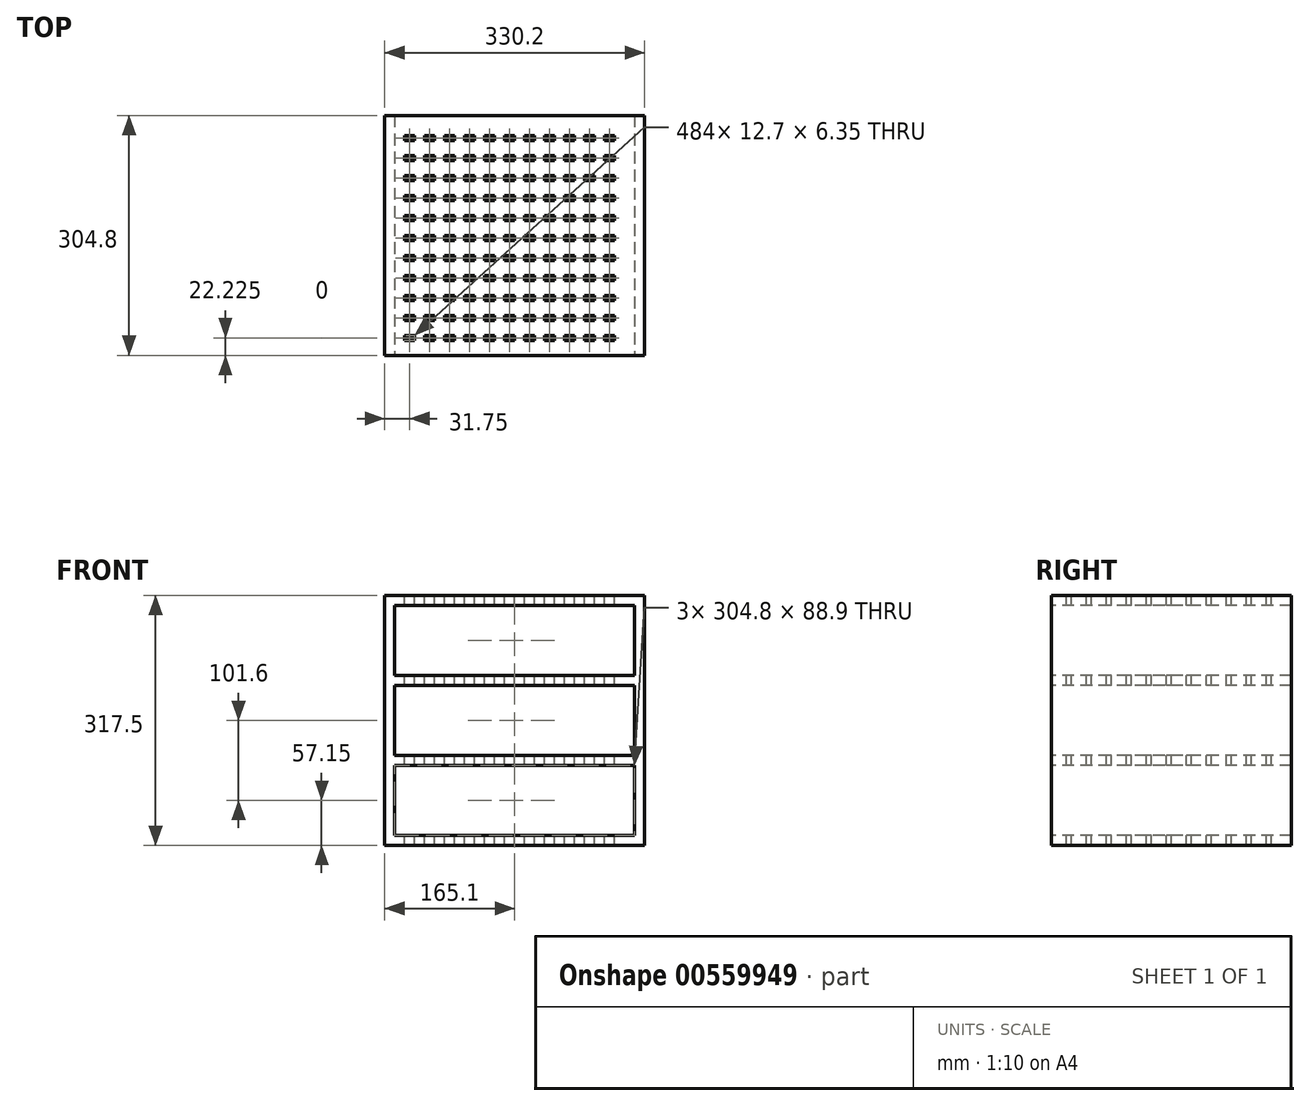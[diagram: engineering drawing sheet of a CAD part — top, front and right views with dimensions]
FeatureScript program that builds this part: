
annotation { "Feature Type Name" : "Feature", "Feature Type Description" : "" }
export const myFeature = defineFeature(function(context is Context, id is Id, definition is map)
    precondition{}
    {
        {
            var Q0;
            Q0=qCreatedBy(makeId("Front.planeOp"),FACE);
            var sketch = newSketch(context, id + "F0", { "sketchPlane" : qUnion([Q0])});
            skLineSegment(sketch, "E0.bottom", {"start": v(0, 88.9) * mm, "end": v(304.8, 88.9) * mm});
            skLineSegment(sketch, "E0.top", {"start": v(0, 0) * mm, "end": v(304.8, 0) * mm});
            skLineSegment(sketch, "E0.left", {"start": v(0, 88.9) * mm, "end": v(0, 0) * mm});
            skLineSegment(sketch, "E0.right", {"start": v(304.8, 88.9) * mm, "end": v(304.8, 0) * mm});
            skLineSegment(sketch, "E1.top", {"start": v(0, 101.6) * mm, "end": v(304.8, 101.6) * mm});
            skLineSegment(sketch, "E2.top", {"start": v(0, 190.5) * mm, "end": v(304.8, 190.5) * mm});
            skLineSegment(sketch, "E2.left", {"start": v(0, 101.6) * mm, "end": v(0, 190.5) * mm});
            skLineSegment(sketch, "E2.right", {"start": v(304.8, 101.6) * mm, "end": v(304.8, 190.5) * mm});
            skLineSegment(sketch, "E3.left", {"start": v(0, 0) * mm, "end": v(0, 88.9) * mm});
            skLineSegment(sketch, "E4.right", {"start": v(304.8, 190.5) * mm, "end": v(304.8, 101.6) * mm});
            skLineSegment(sketch, "E5.top", {"start": v(304.8, 0) * mm, "end": v(0, 0) * mm});
            skLineSegment(sketch, "E6", {"start": v(-12.7, 304.8) * mm, "end": v(-12.7, -12.7) * mm});
            skLineSegment(sketch, "E7", {"start": v(-12.7, -12.7) * mm, "end": v(317.5, -12.7) * mm});
            skLineSegment(sketch, "E8", {"start": v(317.5, -12.7) * mm, "end": v(317.5, 304.8) * mm});
            skLineSegment(sketch, "E9.bottom", {"start": v(0, 203.2) * mm, "end": v(304.8, 203.2) * mm});
            skLineSegment(sketch, "E9.top", {"start": v(0, 292.1) * mm, "end": v(304.8, 292.1) * mm});
            skLineSegment(sketch, "E9.left", {"start": v(0, 203.2) * mm, "end": v(0, 292.1) * mm});
            skLineSegment(sketch, "E9.right", {"start": v(304.8, 203.2) * mm, "end": v(304.8, 292.1) * mm});
            skLineSegment(sketch, "E10", {"start": v(-12.7, 304.8) * mm, "end": v(317.5, 304.8) * mm});
            skSolve(sketch);
        }
        {
            var Q0;
            Q0=makeQuery(id+"F0.imprint","IMPRINT",FACE,{"disambiguationData":[TD([[makeQuery(id+"F0.imprint","IMPRINT",EDGE,{"derivedFrom":sQuery(id+"F0.wireOp",EDGE,"E0.bottom")}),1.0]])]});
            extrude(context, id + "F1", {"entities" : qUnion([Q0]), "oppositeDirection" : true, "depth" : 304.8 * mm, "offsetDistance" : 25.4 * mm});
        }
        {
            var Q0;
            Q0=makeQuery(id+"F1.opExtrude","SWEPT_FACE",FACE,{"disambiguationData":[OSD([sQuery(id+"F0.wireOp",EDGE,"E10")])]});
            var sketch = newSketch(context, id + "F2", { "sketchPlane" : qUnion([Q0])});
            skLineSegment(sketch, "E11.bottom", {"start": v(12.7, 19.05) * mm, "end": v(25.4, 19.05) * mm});
            skLineSegment(sketch, "E11.top", {"start": v(12.7, 25.4) * mm, "end": v(25.4, 25.4) * mm});
            skLineSegment(sketch, "E11.left", {"start": v(12.7, 19.05) * mm, "end": v(12.7, 25.4) * mm});
            skLineSegment(sketch, "E11.right", {"start": v(25.4, 19.05) * mm, "end": v(25.4, 25.4) * mm});
            skLineSegment(sketch, "E12.0.1.0", {"start": v(12.7, 44.45) * mm, "end": v(12.7, 50.8) * mm});
            skLineSegment(sketch, "E12.0.1.1", {"start": v(12.7, 50.8) * mm, "end": v(25.4, 50.8) * mm});
            skLineSegment(sketch, "E12.0.1.2", {"start": v(25.4, 44.45) * mm, "end": v(25.4, 50.8) * mm});
            skLineSegment(sketch, "E12.0.1.3", {"start": v(12.7, 44.45) * mm, "end": v(25.4, 44.45) * mm});
            skLineSegment(sketch, "E12.0.2.0", {"start": v(12.7, 69.85) * mm, "end": v(12.7, 76.2) * mm});
            skLineSegment(sketch, "E12.0.2.1", {"start": v(12.7, 76.2) * mm, "end": v(25.4, 76.2) * mm});
            skLineSegment(sketch, "E12.0.2.2", {"start": v(25.4, 69.85) * mm, "end": v(25.4, 76.2) * mm});
            skLineSegment(sketch, "E12.0.2.3", {"start": v(12.7, 69.85) * mm, "end": v(25.4, 69.85) * mm});
            skLineSegment(sketch, "E12.0.3.0", {"start": v(12.7, 95.25) * mm, "end": v(12.7, 101.6) * mm});
            skLineSegment(sketch, "E12.0.3.1", {"start": v(12.7, 101.6) * mm, "end": v(25.4, 101.6) * mm});
            skLineSegment(sketch, "E12.0.3.2", {"start": v(25.4, 95.25) * mm, "end": v(25.4, 101.6) * mm});
            skLineSegment(sketch, "E12.0.3.3", {"start": v(12.7, 95.25) * mm, "end": v(25.4, 95.25) * mm});
            skLineSegment(sketch, "E12.0.4.0", {"start": v(12.7, 120.65) * mm, "end": v(12.7, 127) * mm});
            skLineSegment(sketch, "E12.0.4.1", {"start": v(12.7, 127) * mm, "end": v(25.4, 127) * mm});
            skLineSegment(sketch, "E12.0.4.2", {"start": v(25.4, 120.65) * mm, "end": v(25.4, 127) * mm});
            skLineSegment(sketch, "E12.0.4.3", {"start": v(12.7, 120.65) * mm, "end": v(25.4, 120.65) * mm});
            skLineSegment(sketch, "E12.0.5.0", {"start": v(12.7, 146.05) * mm, "end": v(12.7, 152.4) * mm});
            skLineSegment(sketch, "E12.0.5.1", {"start": v(12.7, 152.4) * mm, "end": v(25.4, 152.4) * mm});
            skLineSegment(sketch, "E12.0.5.2", {"start": v(25.4, 146.05) * mm, "end": v(25.4, 152.4) * mm});
            skLineSegment(sketch, "E12.0.5.3", {"start": v(12.7, 146.05) * mm, "end": v(25.4, 146.05) * mm});
            skLineSegment(sketch, "E12.0.6.0", {"start": v(12.7, 171.45) * mm, "end": v(12.7, 177.8) * mm});
            skLineSegment(sketch, "E12.0.6.1", {"start": v(12.7, 177.8) * mm, "end": v(25.4, 177.8) * mm});
            skLineSegment(sketch, "E12.0.6.2", {"start": v(25.4, 171.45) * mm, "end": v(25.4, 177.8) * mm});
            skLineSegment(sketch, "E12.0.6.3", {"start": v(12.7, 171.45) * mm, "end": v(25.4, 171.45) * mm});
            skLineSegment(sketch, "E12.0.7.0", {"start": v(12.7, 196.85) * mm, "end": v(12.7, 203.2) * mm});
            skLineSegment(sketch, "E12.0.7.1", {"start": v(12.7, 203.2) * mm, "end": v(25.4, 203.2) * mm});
            skLineSegment(sketch, "E12.0.7.2", {"start": v(25.4, 196.85) * mm, "end": v(25.4, 203.2) * mm});
            skLineSegment(sketch, "E12.0.7.3", {"start": v(12.7, 196.85) * mm, "end": v(25.4, 196.85) * mm});
            skLineSegment(sketch, "E12.0.8.0", {"start": v(12.7, 222.25) * mm, "end": v(12.7, 228.6) * mm});
            skLineSegment(sketch, "E12.0.8.1", {"start": v(12.7, 228.6) * mm, "end": v(25.4, 228.6) * mm});
            skLineSegment(sketch, "E12.0.8.2", {"start": v(25.4, 222.25) * mm, "end": v(25.4, 228.6) * mm});
            skLineSegment(sketch, "E12.0.8.3", {"start": v(12.7, 222.25) * mm, "end": v(25.4, 222.25) * mm});
            skLineSegment(sketch, "E12.0.9.0", {"start": v(12.7, 247.65) * mm, "end": v(12.7, 254) * mm});
            skLineSegment(sketch, "E12.0.9.1", {"start": v(12.7, 254) * mm, "end": v(25.4, 254) * mm});
            skLineSegment(sketch, "E12.0.9.2", {"start": v(25.4, 247.65) * mm, "end": v(25.4, 254) * mm});
            skLineSegment(sketch, "E12.0.9.3", {"start": v(12.7, 247.65) * mm, "end": v(25.4, 247.65) * mm});
            skLineSegment(sketch, "E12.0.10.0", {"start": v(12.7, 273.05) * mm, "end": v(12.7, 279.4) * mm});
            skLineSegment(sketch, "E12.0.10.1", {"start": v(12.7, 279.4) * mm, "end": v(25.4, 279.4) * mm});
            skLineSegment(sketch, "E12.0.10.2", {"start": v(25.4, 273.05) * mm, "end": v(25.4, 279.4) * mm});
            skLineSegment(sketch, "E12.0.10.3", {"start": v(12.7, 273.05) * mm, "end": v(25.4, 273.05) * mm});
            skLineSegment(sketch, "E12.1.0.0", {"start": v(38.1, 19.05) * mm, "end": v(38.1, 25.4) * mm});
            skLineSegment(sketch, "E12.1.0.1", {"start": v(38.1, 25.4) * mm, "end": v(50.8, 25.4) * mm});
            skLineSegment(sketch, "E12.1.0.2", {"start": v(50.8, 19.05) * mm, "end": v(50.8, 25.4) * mm});
            skLineSegment(sketch, "E12.1.0.3", {"start": v(38.1, 19.05) * mm, "end": v(50.8, 19.05) * mm});
            skLineSegment(sketch, "E12.1.1.0", {"start": v(38.1, 44.45) * mm, "end": v(38.1, 50.8) * mm});
            skLineSegment(sketch, "E12.1.1.1", {"start": v(38.1, 50.8) * mm, "end": v(50.8, 50.8) * mm});
            skLineSegment(sketch, "E12.1.1.2", {"start": v(50.8, 44.45) * mm, "end": v(50.8, 50.8) * mm});
            skLineSegment(sketch, "E12.1.1.3", {"start": v(38.1, 44.45) * mm, "end": v(50.8, 44.45) * mm});
            skLineSegment(sketch, "E12.1.2.0", {"start": v(38.1, 69.85) * mm, "end": v(38.1, 76.2) * mm});
            skLineSegment(sketch, "E12.1.2.1", {"start": v(38.1, 76.2) * mm, "end": v(50.8, 76.2) * mm});
            skLineSegment(sketch, "E12.1.2.2", {"start": v(50.8, 69.85) * mm, "end": v(50.8, 76.2) * mm});
            skLineSegment(sketch, "E12.1.2.3", {"start": v(38.1, 69.85) * mm, "end": v(50.8, 69.85) * mm});
            skLineSegment(sketch, "E12.1.3.0", {"start": v(38.1, 95.25) * mm, "end": v(38.1, 101.6) * mm});
            skLineSegment(sketch, "E12.1.3.1", {"start": v(38.1, 101.6) * mm, "end": v(50.8, 101.6) * mm});
            skLineSegment(sketch, "E12.1.3.2", {"start": v(50.8, 95.25) * mm, "end": v(50.8, 101.6) * mm});
            skLineSegment(sketch, "E12.1.3.3", {"start": v(38.1, 95.25) * mm, "end": v(50.8, 95.25) * mm});
            skLineSegment(sketch, "E12.1.4.0", {"start": v(38.1, 120.65) * mm, "end": v(38.1, 127) * mm});
            skLineSegment(sketch, "E12.1.4.1", {"start": v(38.1, 127) * mm, "end": v(50.8, 127) * mm});
            skLineSegment(sketch, "E12.1.4.2", {"start": v(50.8, 120.65) * mm, "end": v(50.8, 127) * mm});
            skLineSegment(sketch, "E12.1.4.3", {"start": v(38.1, 120.65) * mm, "end": v(50.8, 120.65) * mm});
            skLineSegment(sketch, "E12.1.5.0", {"start": v(38.1, 146.05) * mm, "end": v(38.1, 152.4) * mm});
            skLineSegment(sketch, "E12.1.5.1", {"start": v(38.1, 152.4) * mm, "end": v(50.8, 152.4) * mm});
            skLineSegment(sketch, "E12.1.5.2", {"start": v(50.8, 146.05) * mm, "end": v(50.8, 152.4) * mm});
            skLineSegment(sketch, "E12.1.5.3", {"start": v(38.1, 146.05) * mm, "end": v(50.8, 146.05) * mm});
            skLineSegment(sketch, "E12.1.6.0", {"start": v(38.1, 171.45) * mm, "end": v(38.1, 177.8) * mm});
            skLineSegment(sketch, "E12.1.6.1", {"start": v(38.1, 177.8) * mm, "end": v(50.8, 177.8) * mm});
            skLineSegment(sketch, "E12.1.6.2", {"start": v(50.8, 171.45) * mm, "end": v(50.8, 177.8) * mm});
            skLineSegment(sketch, "E12.1.6.3", {"start": v(38.1, 171.45) * mm, "end": v(50.8, 171.45) * mm});
            skLineSegment(sketch, "E12.1.7.0", {"start": v(38.1, 196.85) * mm, "end": v(38.1, 203.2) * mm});
            skLineSegment(sketch, "E12.1.7.1", {"start": v(38.1, 203.2) * mm, "end": v(50.8, 203.2) * mm});
            skLineSegment(sketch, "E12.1.7.2", {"start": v(50.8, 196.85) * mm, "end": v(50.8, 203.2) * mm});
            skLineSegment(sketch, "E12.1.7.3", {"start": v(38.1, 196.85) * mm, "end": v(50.8, 196.85) * mm});
            skLineSegment(sketch, "E12.1.8.0", {"start": v(38.1, 222.25) * mm, "end": v(38.1, 228.6) * mm});
            skLineSegment(sketch, "E12.1.8.1", {"start": v(38.1, 228.6) * mm, "end": v(50.8, 228.6) * mm});
            skLineSegment(sketch, "E12.1.8.2", {"start": v(50.8, 222.25) * mm, "end": v(50.8, 228.6) * mm});
            skLineSegment(sketch, "E12.1.8.3", {"start": v(38.1, 222.25) * mm, "end": v(50.8, 222.25) * mm});
            skLineSegment(sketch, "E12.1.9.0", {"start": v(38.1, 247.65) * mm, "end": v(38.1, 254) * mm});
            skLineSegment(sketch, "E12.1.9.1", {"start": v(38.1, 254) * mm, "end": v(50.8, 254) * mm});
            skLineSegment(sketch, "E12.1.9.2", {"start": v(50.8, 247.65) * mm, "end": v(50.8, 254) * mm});
            skLineSegment(sketch, "E12.1.9.3", {"start": v(38.1, 247.65) * mm, "end": v(50.8, 247.65) * mm});
            skLineSegment(sketch, "E12.1.10.0", {"start": v(38.1, 273.05) * mm, "end": v(38.1, 279.4) * mm});
            skLineSegment(sketch, "E12.1.10.1", {"start": v(38.1, 279.4) * mm, "end": v(50.8, 279.4) * mm});
            skLineSegment(sketch, "E12.1.10.2", {"start": v(50.8, 273.05) * mm, "end": v(50.8, 279.4) * mm});
            skLineSegment(sketch, "E12.1.10.3", {"start": v(38.1, 273.05) * mm, "end": v(50.8, 273.05) * mm});
            skLineSegment(sketch, "E12.2.0.0", {"start": v(63.5, 19.05) * mm, "end": v(63.5, 25.4) * mm});
            skLineSegment(sketch, "E12.2.0.1", {"start": v(63.5, 25.4) * mm, "end": v(76.2, 25.4) * mm});
            skLineSegment(sketch, "E12.2.0.2", {"start": v(76.2, 19.05) * mm, "end": v(76.2, 25.4) * mm});
            skLineSegment(sketch, "E12.2.0.3", {"start": v(63.5, 19.05) * mm, "end": v(76.2, 19.05) * mm});
            skLineSegment(sketch, "E12.2.1.0", {"start": v(63.5, 44.45) * mm, "end": v(63.5, 50.8) * mm});
            skLineSegment(sketch, "E12.2.1.1", {"start": v(63.5, 50.8) * mm, "end": v(76.2, 50.8) * mm});
            skLineSegment(sketch, "E12.2.1.2", {"start": v(76.2, 44.45) * mm, "end": v(76.2, 50.8) * mm});
            skLineSegment(sketch, "E12.2.1.3", {"start": v(63.5, 44.45) * mm, "end": v(76.2, 44.45) * mm});
            skLineSegment(sketch, "E12.2.2.0", {"start": v(63.5, 69.85) * mm, "end": v(63.5, 76.2) * mm});
            skLineSegment(sketch, "E12.2.2.1", {"start": v(63.5, 76.2) * mm, "end": v(76.2, 76.2) * mm});
            skLineSegment(sketch, "E12.2.2.2", {"start": v(76.2, 69.85) * mm, "end": v(76.2, 76.2) * mm});
            skLineSegment(sketch, "E12.2.2.3", {"start": v(63.5, 69.85) * mm, "end": v(76.2, 69.85) * mm});
            skLineSegment(sketch, "E12.2.3.0", {"start": v(63.5, 95.25) * mm, "end": v(63.5, 101.6) * mm});
            skLineSegment(sketch, "E12.2.3.1", {"start": v(63.5, 101.6) * mm, "end": v(76.2, 101.6) * mm});
            skLineSegment(sketch, "E12.2.3.2", {"start": v(76.2, 95.25) * mm, "end": v(76.2, 101.6) * mm});
            skLineSegment(sketch, "E12.2.3.3", {"start": v(63.5, 95.25) * mm, "end": v(76.2, 95.25) * mm});
            skLineSegment(sketch, "E12.2.4.0", {"start": v(63.5, 120.65) * mm, "end": v(63.5, 127) * mm});
            skLineSegment(sketch, "E12.2.4.1", {"start": v(63.5, 127) * mm, "end": v(76.2, 127) * mm});
            skLineSegment(sketch, "E12.2.4.2", {"start": v(76.2, 120.65) * mm, "end": v(76.2, 127) * mm});
            skLineSegment(sketch, "E12.2.4.3", {"start": v(63.5, 120.65) * mm, "end": v(76.2, 120.65) * mm});
            skLineSegment(sketch, "E12.2.5.0", {"start": v(63.5, 146.05) * mm, "end": v(63.5, 152.4) * mm});
            skLineSegment(sketch, "E12.2.5.1", {"start": v(63.5, 152.4) * mm, "end": v(76.2, 152.4) * mm});
            skLineSegment(sketch, "E12.2.5.2", {"start": v(76.2, 146.05) * mm, "end": v(76.2, 152.4) * mm});
            skLineSegment(sketch, "E12.2.5.3", {"start": v(63.5, 146.05) * mm, "end": v(76.2, 146.05) * mm});
            skLineSegment(sketch, "E12.2.6.0", {"start": v(63.5, 171.45) * mm, "end": v(63.5, 177.8) * mm});
            skLineSegment(sketch, "E12.2.6.1", {"start": v(63.5, 177.8) * mm, "end": v(76.2, 177.8) * mm});
            skLineSegment(sketch, "E12.2.6.2", {"start": v(76.2, 171.45) * mm, "end": v(76.2, 177.8) * mm});
            skLineSegment(sketch, "E12.2.6.3", {"start": v(63.5, 171.45) * mm, "end": v(76.2, 171.45) * mm});
            skLineSegment(sketch, "E12.2.7.0", {"start": v(63.5, 196.85) * mm, "end": v(63.5, 203.2) * mm});
            skLineSegment(sketch, "E12.2.7.1", {"start": v(63.5, 203.2) * mm, "end": v(76.2, 203.2) * mm});
            skLineSegment(sketch, "E12.2.7.2", {"start": v(76.2, 196.85) * mm, "end": v(76.2, 203.2) * mm});
            skLineSegment(sketch, "E12.2.7.3", {"start": v(63.5, 196.85) * mm, "end": v(76.2, 196.85) * mm});
            skLineSegment(sketch, "E12.2.8.0", {"start": v(63.5, 222.25) * mm, "end": v(63.5, 228.6) * mm});
            skLineSegment(sketch, "E12.2.8.1", {"start": v(63.5, 228.6) * mm, "end": v(76.2, 228.6) * mm});
            skLineSegment(sketch, "E12.2.8.2", {"start": v(76.2, 222.25) * mm, "end": v(76.2, 228.6) * mm});
            skLineSegment(sketch, "E12.2.8.3", {"start": v(63.5, 222.25) * mm, "end": v(76.2, 222.25) * mm});
            skLineSegment(sketch, "E12.2.9.0", {"start": v(63.5, 247.65) * mm, "end": v(63.5, 254) * mm});
            skLineSegment(sketch, "E12.2.9.1", {"start": v(63.5, 254) * mm, "end": v(76.2, 254) * mm});
            skLineSegment(sketch, "E12.2.9.2", {"start": v(76.2, 247.65) * mm, "end": v(76.2, 254) * mm});
            skLineSegment(sketch, "E12.2.9.3", {"start": v(63.5, 247.65) * mm, "end": v(76.2, 247.65) * mm});
            skLineSegment(sketch, "E12.2.10.0", {"start": v(63.5, 273.05) * mm, "end": v(63.5, 279.4) * mm});
            skLineSegment(sketch, "E12.2.10.1", {"start": v(63.5, 279.4) * mm, "end": v(76.2, 279.4) * mm});
            skLineSegment(sketch, "E12.2.10.2", {"start": v(76.2, 273.05) * mm, "end": v(76.2, 279.4) * mm});
            skLineSegment(sketch, "E12.2.10.3", {"start": v(63.5, 273.05) * mm, "end": v(76.2, 273.05) * mm});
            skLineSegment(sketch, "E12.3.0.0", {"start": v(88.9, 19.05) * mm, "end": v(88.9, 25.4) * mm});
            skLineSegment(sketch, "E12.3.0.1", {"start": v(88.9, 25.4) * mm, "end": v(101.6, 25.4) * mm});
            skLineSegment(sketch, "E12.3.0.2", {"start": v(101.6, 19.05) * mm, "end": v(101.6, 25.4) * mm});
            skLineSegment(sketch, "E12.3.0.3", {"start": v(88.9, 19.05) * mm, "end": v(101.6, 19.05) * mm});
            skLineSegment(sketch, "E12.3.1.0", {"start": v(88.9, 44.45) * mm, "end": v(88.9, 50.8) * mm});
            skLineSegment(sketch, "E12.3.1.1", {"start": v(88.9, 50.8) * mm, "end": v(101.6, 50.8) * mm});
            skLineSegment(sketch, "E12.3.1.2", {"start": v(101.6, 44.45) * mm, "end": v(101.6, 50.8) * mm});
            skLineSegment(sketch, "E12.3.1.3", {"start": v(88.9, 44.45) * mm, "end": v(101.6, 44.45) * mm});
            skLineSegment(sketch, "E12.3.2.0", {"start": v(88.9, 69.85) * mm, "end": v(88.9, 76.2) * mm});
            skLineSegment(sketch, "E12.3.2.1", {"start": v(88.9, 76.2) * mm, "end": v(101.6, 76.2) * mm});
            skLineSegment(sketch, "E12.3.2.2", {"start": v(101.6, 69.85) * mm, "end": v(101.6, 76.2) * mm});
            skLineSegment(sketch, "E12.3.2.3", {"start": v(88.9, 69.85) * mm, "end": v(101.6, 69.85) * mm});
            skLineSegment(sketch, "E12.3.3.0", {"start": v(88.9, 95.25) * mm, "end": v(88.9, 101.6) * mm});
            skLineSegment(sketch, "E12.3.3.1", {"start": v(88.9, 101.6) * mm, "end": v(101.6, 101.6) * mm});
            skLineSegment(sketch, "E12.3.3.2", {"start": v(101.6, 95.25) * mm, "end": v(101.6, 101.6) * mm});
            skLineSegment(sketch, "E12.3.3.3", {"start": v(88.9, 95.25) * mm, "end": v(101.6, 95.25) * mm});
            skLineSegment(sketch, "E12.3.4.0", {"start": v(88.9, 120.65) * mm, "end": v(88.9, 127) * mm});
            skLineSegment(sketch, "E12.3.4.1", {"start": v(88.9, 127) * mm, "end": v(101.6, 127) * mm});
            skLineSegment(sketch, "E12.3.4.2", {"start": v(101.6, 120.65) * mm, "end": v(101.6, 127) * mm});
            skLineSegment(sketch, "E12.3.4.3", {"start": v(88.9, 120.65) * mm, "end": v(101.6, 120.65) * mm});
            skLineSegment(sketch, "E12.3.5.0", {"start": v(88.9, 146.05) * mm, "end": v(88.9, 152.4) * mm});
            skLineSegment(sketch, "E12.3.5.1", {"start": v(88.9, 152.4) * mm, "end": v(101.6, 152.4) * mm});
            skLineSegment(sketch, "E12.3.5.2", {"start": v(101.6, 146.05) * mm, "end": v(101.6, 152.4) * mm});
            skLineSegment(sketch, "E12.3.5.3", {"start": v(88.9, 146.05) * mm, "end": v(101.6, 146.05) * mm});
            skLineSegment(sketch, "E12.3.6.0", {"start": v(88.9, 171.45) * mm, "end": v(88.9, 177.8) * mm});
            skLineSegment(sketch, "E12.3.6.1", {"start": v(88.9, 177.8) * mm, "end": v(101.6, 177.8) * mm});
            skLineSegment(sketch, "E12.3.6.2", {"start": v(101.6, 171.45) * mm, "end": v(101.6, 177.8) * mm});
            skLineSegment(sketch, "E12.3.6.3", {"start": v(88.9, 171.45) * mm, "end": v(101.6, 171.45) * mm});
            skLineSegment(sketch, "E12.3.7.0", {"start": v(88.9, 196.85) * mm, "end": v(88.9, 203.2) * mm});
            skLineSegment(sketch, "E12.3.7.1", {"start": v(88.9, 203.2) * mm, "end": v(101.6, 203.2) * mm});
            skLineSegment(sketch, "E12.3.7.2", {"start": v(101.6, 196.85) * mm, "end": v(101.6, 203.2) * mm});
            skLineSegment(sketch, "E12.3.7.3", {"start": v(88.9, 196.85) * mm, "end": v(101.6, 196.85) * mm});
            skLineSegment(sketch, "E12.3.8.0", {"start": v(88.9, 222.25) * mm, "end": v(88.9, 228.6) * mm});
            skLineSegment(sketch, "E12.3.8.1", {"start": v(88.9, 228.6) * mm, "end": v(101.6, 228.6) * mm});
            skLineSegment(sketch, "E12.3.8.2", {"start": v(101.6, 222.25) * mm, "end": v(101.6, 228.6) * mm});
            skLineSegment(sketch, "E12.3.8.3", {"start": v(88.9, 222.25) * mm, "end": v(101.6, 222.25) * mm});
            skLineSegment(sketch, "E12.3.9.0", {"start": v(88.9, 247.65) * mm, "end": v(88.9, 254) * mm});
            skLineSegment(sketch, "E12.3.9.1", {"start": v(88.9, 254) * mm, "end": v(101.6, 254) * mm});
            skLineSegment(sketch, "E12.3.9.2", {"start": v(101.6, 247.65) * mm, "end": v(101.6, 254) * mm});
            skLineSegment(sketch, "E12.3.9.3", {"start": v(88.9, 247.65) * mm, "end": v(101.6, 247.65) * mm});
            skLineSegment(sketch, "E12.3.10.0", {"start": v(88.9, 273.05) * mm, "end": v(88.9, 279.4) * mm});
            skLineSegment(sketch, "E12.3.10.1", {"start": v(88.9, 279.4) * mm, "end": v(101.6, 279.4) * mm});
            skLineSegment(sketch, "E12.3.10.2", {"start": v(101.6, 273.05) * mm, "end": v(101.6, 279.4) * mm});
            skLineSegment(sketch, "E12.3.10.3", {"start": v(88.9, 273.05) * mm, "end": v(101.6, 273.05) * mm});
            skLineSegment(sketch, "E12.4.0.0", {"start": v(114.3, 19.05) * mm, "end": v(114.3, 25.4) * mm});
            skLineSegment(sketch, "E12.4.0.1", {"start": v(114.3, 25.4) * mm, "end": v(127, 25.4) * mm});
            skLineSegment(sketch, "E12.4.0.2", {"start": v(127, 19.05) * mm, "end": v(127, 25.4) * mm});
            skLineSegment(sketch, "E12.4.0.3", {"start": v(114.3, 19.05) * mm, "end": v(127, 19.05) * mm});
            skLineSegment(sketch, "E12.4.1.0", {"start": v(114.3, 44.45) * mm, "end": v(114.3, 50.8) * mm});
            skLineSegment(sketch, "E12.4.1.1", {"start": v(114.3, 50.8) * mm, "end": v(127, 50.8) * mm});
            skLineSegment(sketch, "E12.4.1.2", {"start": v(127, 44.45) * mm, "end": v(127, 50.8) * mm});
            skLineSegment(sketch, "E12.4.1.3", {"start": v(114.3, 44.45) * mm, "end": v(127, 44.45) * mm});
            skLineSegment(sketch, "E12.4.2.0", {"start": v(114.3, 69.85) * mm, "end": v(114.3, 76.2) * mm});
            skLineSegment(sketch, "E12.4.2.1", {"start": v(114.3, 76.2) * mm, "end": v(127, 76.2) * mm});
            skLineSegment(sketch, "E12.4.2.2", {"start": v(127, 69.85) * mm, "end": v(127, 76.2) * mm});
            skLineSegment(sketch, "E12.4.2.3", {"start": v(114.3, 69.85) * mm, "end": v(127, 69.85) * mm});
            skLineSegment(sketch, "E12.4.3.0", {"start": v(114.3, 95.25) * mm, "end": v(114.3, 101.6) * mm});
            skLineSegment(sketch, "E12.4.3.1", {"start": v(114.3, 101.6) * mm, "end": v(127, 101.6) * mm});
            skLineSegment(sketch, "E12.4.3.2", {"start": v(127, 95.25) * mm, "end": v(127, 101.6) * mm});
            skLineSegment(sketch, "E12.4.3.3", {"start": v(114.3, 95.25) * mm, "end": v(127, 95.25) * mm});
            skLineSegment(sketch, "E12.4.4.0", {"start": v(114.3, 120.65) * mm, "end": v(114.3, 127) * mm});
            skLineSegment(sketch, "E12.4.4.1", {"start": v(114.3, 127) * mm, "end": v(127, 127) * mm});
            skLineSegment(sketch, "E12.4.4.2", {"start": v(127, 120.65) * mm, "end": v(127, 127) * mm});
            skLineSegment(sketch, "E12.4.4.3", {"start": v(114.3, 120.65) * mm, "end": v(127, 120.65) * mm});
            skLineSegment(sketch, "E12.4.5.0", {"start": v(114.3, 146.05) * mm, "end": v(114.3, 152.4) * mm});
            skLineSegment(sketch, "E12.4.5.1", {"start": v(114.3, 152.4) * mm, "end": v(127, 152.4) * mm});
            skLineSegment(sketch, "E12.4.5.2", {"start": v(127, 146.05) * mm, "end": v(127, 152.4) * mm});
            skLineSegment(sketch, "E12.4.5.3", {"start": v(114.3, 146.05) * mm, "end": v(127, 146.05) * mm});
            skLineSegment(sketch, "E12.4.6.0", {"start": v(114.3, 171.45) * mm, "end": v(114.3, 177.8) * mm});
            skLineSegment(sketch, "E12.4.6.1", {"start": v(114.3, 177.8) * mm, "end": v(127, 177.8) * mm});
            skLineSegment(sketch, "E12.4.6.2", {"start": v(127, 171.45) * mm, "end": v(127, 177.8) * mm});
            skLineSegment(sketch, "E12.4.6.3", {"start": v(114.3, 171.45) * mm, "end": v(127, 171.45) * mm});
            skLineSegment(sketch, "E12.4.7.0", {"start": v(114.3, 196.85) * mm, "end": v(114.3, 203.2) * mm});
            skLineSegment(sketch, "E12.4.7.1", {"start": v(114.3, 203.2) * mm, "end": v(127, 203.2) * mm});
            skLineSegment(sketch, "E12.4.7.2", {"start": v(127, 196.85) * mm, "end": v(127, 203.2) * mm});
            skLineSegment(sketch, "E12.4.7.3", {"start": v(114.3, 196.85) * mm, "end": v(127, 196.85) * mm});
            skLineSegment(sketch, "E12.4.8.0", {"start": v(114.3, 222.25) * mm, "end": v(114.3, 228.6) * mm});
            skLineSegment(sketch, "E12.4.8.1", {"start": v(114.3, 228.6) * mm, "end": v(127, 228.6) * mm});
            skLineSegment(sketch, "E12.4.8.2", {"start": v(127, 222.25) * mm, "end": v(127, 228.6) * mm});
            skLineSegment(sketch, "E12.4.8.3", {"start": v(114.3, 222.25) * mm, "end": v(127, 222.25) * mm});
            skLineSegment(sketch, "E12.4.9.0", {"start": v(114.3, 247.65) * mm, "end": v(114.3, 254) * mm});
            skLineSegment(sketch, "E12.4.9.1", {"start": v(114.3, 254) * mm, "end": v(127, 254) * mm});
            skLineSegment(sketch, "E12.4.9.2", {"start": v(127, 247.65) * mm, "end": v(127, 254) * mm});
            skLineSegment(sketch, "E12.4.9.3", {"start": v(114.3, 247.65) * mm, "end": v(127, 247.65) * mm});
            skLineSegment(sketch, "E12.4.10.0", {"start": v(114.3, 273.05) * mm, "end": v(114.3, 279.4) * mm});
            skLineSegment(sketch, "E12.4.10.1", {"start": v(114.3, 279.4) * mm, "end": v(127, 279.4) * mm});
            skLineSegment(sketch, "E12.4.10.2", {"start": v(127, 273.05) * mm, "end": v(127, 279.4) * mm});
            skLineSegment(sketch, "E12.4.10.3", {"start": v(114.3, 273.05) * mm, "end": v(127, 273.05) * mm});
            skLineSegment(sketch, "E12.5.0.0", {"start": v(139.7, 19.05) * mm, "end": v(139.7, 25.4) * mm});
            skLineSegment(sketch, "E12.5.0.1", {"start": v(139.7, 25.4) * mm, "end": v(152.4, 25.4) * mm});
            skLineSegment(sketch, "E12.5.0.2", {"start": v(152.4, 19.05) * mm, "end": v(152.4, 25.4) * mm});
            skLineSegment(sketch, "E12.5.0.3", {"start": v(139.7, 19.05) * mm, "end": v(152.4, 19.05) * mm});
            skLineSegment(sketch, "E12.5.1.0", {"start": v(139.7, 44.45) * mm, "end": v(139.7, 50.8) * mm});
            skLineSegment(sketch, "E12.5.1.1", {"start": v(139.7, 50.8) * mm, "end": v(152.4, 50.8) * mm});
            skLineSegment(sketch, "E12.5.1.2", {"start": v(152.4, 44.45) * mm, "end": v(152.4, 50.8) * mm});
            skLineSegment(sketch, "E12.5.1.3", {"start": v(139.7, 44.45) * mm, "end": v(152.4, 44.45) * mm});
            skLineSegment(sketch, "E12.5.2.0", {"start": v(139.7, 69.85) * mm, "end": v(139.7, 76.2) * mm});
            skLineSegment(sketch, "E12.5.2.1", {"start": v(139.7, 76.2) * mm, "end": v(152.4, 76.2) * mm});
            skLineSegment(sketch, "E12.5.2.2", {"start": v(152.4, 69.85) * mm, "end": v(152.4, 76.2) * mm});
            skLineSegment(sketch, "E12.5.2.3", {"start": v(139.7, 69.85) * mm, "end": v(152.4, 69.85) * mm});
            skLineSegment(sketch, "E12.5.3.0", {"start": v(139.7, 95.25) * mm, "end": v(139.7, 101.6) * mm});
            skLineSegment(sketch, "E12.5.3.1", {"start": v(139.7, 101.6) * mm, "end": v(152.4, 101.6) * mm});
            skLineSegment(sketch, "E12.5.3.2", {"start": v(152.4, 95.25) * mm, "end": v(152.4, 101.6) * mm});
            skLineSegment(sketch, "E12.5.3.3", {"start": v(139.7, 95.25) * mm, "end": v(152.4, 95.25) * mm});
            skLineSegment(sketch, "E12.5.4.0", {"start": v(139.7, 120.65) * mm, "end": v(139.7, 127) * mm});
            skLineSegment(sketch, "E12.5.4.1", {"start": v(139.7, 127) * mm, "end": v(152.4, 127) * mm});
            skLineSegment(sketch, "E12.5.4.2", {"start": v(152.4, 120.65) * mm, "end": v(152.4, 127) * mm});
            skLineSegment(sketch, "E12.5.4.3", {"start": v(139.7, 120.65) * mm, "end": v(152.4, 120.65) * mm});
            skLineSegment(sketch, "E12.5.5.0", {"start": v(139.7, 146.05) * mm, "end": v(139.7, 152.4) * mm});
            skLineSegment(sketch, "E12.5.5.1", {"start": v(139.7, 152.4) * mm, "end": v(152.4, 152.4) * mm});
            skLineSegment(sketch, "E12.5.5.2", {"start": v(152.4, 146.05) * mm, "end": v(152.4, 152.4) * mm});
            skLineSegment(sketch, "E12.5.5.3", {"start": v(139.7, 146.05) * mm, "end": v(152.4, 146.05) * mm});
            skLineSegment(sketch, "E12.5.6.0", {"start": v(139.7, 171.45) * mm, "end": v(139.7, 177.8) * mm});
            skLineSegment(sketch, "E12.5.6.1", {"start": v(139.7, 177.8) * mm, "end": v(152.4, 177.8) * mm});
            skLineSegment(sketch, "E12.5.6.2", {"start": v(152.4, 171.45) * mm, "end": v(152.4, 177.8) * mm});
            skLineSegment(sketch, "E12.5.6.3", {"start": v(139.7, 171.45) * mm, "end": v(152.4, 171.45) * mm});
            skLineSegment(sketch, "E12.5.7.0", {"start": v(139.7, 196.85) * mm, "end": v(139.7, 203.2) * mm});
            skLineSegment(sketch, "E12.5.7.1", {"start": v(139.7, 203.2) * mm, "end": v(152.4, 203.2) * mm});
            skLineSegment(sketch, "E12.5.7.2", {"start": v(152.4, 196.85) * mm, "end": v(152.4, 203.2) * mm});
            skLineSegment(sketch, "E12.5.7.3", {"start": v(139.7, 196.85) * mm, "end": v(152.4, 196.85) * mm});
            skLineSegment(sketch, "E12.5.8.0", {"start": v(139.7, 222.25) * mm, "end": v(139.7, 228.6) * mm});
            skLineSegment(sketch, "E12.5.8.1", {"start": v(139.7, 228.6) * mm, "end": v(152.4, 228.6) * mm});
            skLineSegment(sketch, "E12.5.8.2", {"start": v(152.4, 222.25) * mm, "end": v(152.4, 228.6) * mm});
            skLineSegment(sketch, "E12.5.8.3", {"start": v(139.7, 222.25) * mm, "end": v(152.4, 222.25) * mm});
            skLineSegment(sketch, "E12.5.9.0", {"start": v(139.7, 247.65) * mm, "end": v(139.7, 254) * mm});
            skLineSegment(sketch, "E12.5.9.1", {"start": v(139.7, 254) * mm, "end": v(152.4, 254) * mm});
            skLineSegment(sketch, "E12.5.9.2", {"start": v(152.4, 247.65) * mm, "end": v(152.4, 254) * mm});
            skLineSegment(sketch, "E12.5.9.3", {"start": v(139.7, 247.65) * mm, "end": v(152.4, 247.65) * mm});
            skLineSegment(sketch, "E12.5.10.0", {"start": v(139.7, 273.05) * mm, "end": v(139.7, 279.4) * mm});
            skLineSegment(sketch, "E12.5.10.1", {"start": v(139.7, 279.4) * mm, "end": v(152.4, 279.4) * mm});
            skLineSegment(sketch, "E12.5.10.2", {"start": v(152.4, 273.05) * mm, "end": v(152.4, 279.4) * mm});
            skLineSegment(sketch, "E12.5.10.3", {"start": v(139.7, 273.05) * mm, "end": v(152.4, 273.05) * mm});
            skLineSegment(sketch, "E12.6.0.0", {"start": v(165.1, 19.05) * mm, "end": v(165.1, 25.4) * mm});
            skLineSegment(sketch, "E12.6.0.1", {"start": v(165.1, 25.4) * mm, "end": v(177.8, 25.4) * mm});
            skLineSegment(sketch, "E12.6.0.2", {"start": v(177.8, 19.05) * mm, "end": v(177.8, 25.4) * mm});
            skLineSegment(sketch, "E12.6.0.3", {"start": v(165.1, 19.05) * mm, "end": v(177.8, 19.05) * mm});
            skLineSegment(sketch, "E12.6.1.0", {"start": v(165.1, 44.45) * mm, "end": v(165.1, 50.8) * mm});
            skLineSegment(sketch, "E12.6.1.1", {"start": v(165.1, 50.8) * mm, "end": v(177.8, 50.8) * mm});
            skLineSegment(sketch, "E12.6.1.2", {"start": v(177.8, 44.45) * mm, "end": v(177.8, 50.8) * mm});
            skLineSegment(sketch, "E12.6.1.3", {"start": v(165.1, 44.45) * mm, "end": v(177.8, 44.45) * mm});
            skLineSegment(sketch, "E12.6.2.0", {"start": v(165.1, 69.85) * mm, "end": v(165.1, 76.2) * mm});
            skLineSegment(sketch, "E12.6.2.1", {"start": v(165.1, 76.2) * mm, "end": v(177.8, 76.2) * mm});
            skLineSegment(sketch, "E12.6.2.2", {"start": v(177.8, 69.85) * mm, "end": v(177.8, 76.2) * mm});
            skLineSegment(sketch, "E12.6.2.3", {"start": v(165.1, 69.85) * mm, "end": v(177.8, 69.85) * mm});
            skLineSegment(sketch, "E12.6.3.0", {"start": v(165.1, 95.25) * mm, "end": v(165.1, 101.6) * mm});
            skLineSegment(sketch, "E12.6.3.1", {"start": v(165.1, 101.6) * mm, "end": v(177.8, 101.6) * mm});
            skLineSegment(sketch, "E12.6.3.2", {"start": v(177.8, 95.25) * mm, "end": v(177.8, 101.6) * mm});
            skLineSegment(sketch, "E12.6.3.3", {"start": v(165.1, 95.25) * mm, "end": v(177.8, 95.25) * mm});
            skLineSegment(sketch, "E12.6.4.0", {"start": v(165.1, 120.65) * mm, "end": v(165.1, 127) * mm});
            skLineSegment(sketch, "E12.6.4.1", {"start": v(165.1, 127) * mm, "end": v(177.8, 127) * mm});
            skLineSegment(sketch, "E12.6.4.2", {"start": v(177.8, 120.65) * mm, "end": v(177.8, 127) * mm});
            skLineSegment(sketch, "E12.6.4.3", {"start": v(165.1, 120.65) * mm, "end": v(177.8, 120.65) * mm});
            skLineSegment(sketch, "E12.6.5.0", {"start": v(165.1, 146.05) * mm, "end": v(165.1, 152.4) * mm});
            skLineSegment(sketch, "E12.6.5.1", {"start": v(165.1, 152.4) * mm, "end": v(177.8, 152.4) * mm});
            skLineSegment(sketch, "E12.6.5.2", {"start": v(177.8, 146.05) * mm, "end": v(177.8, 152.4) * mm});
            skLineSegment(sketch, "E12.6.5.3", {"start": v(165.1, 146.05) * mm, "end": v(177.8, 146.05) * mm});
            skLineSegment(sketch, "E12.6.6.0", {"start": v(165.1, 171.45) * mm, "end": v(165.1, 177.8) * mm});
            skLineSegment(sketch, "E12.6.6.1", {"start": v(165.1, 177.8) * mm, "end": v(177.8, 177.8) * mm});
            skLineSegment(sketch, "E12.6.6.2", {"start": v(177.8, 171.45) * mm, "end": v(177.8, 177.8) * mm});
            skLineSegment(sketch, "E12.6.6.3", {"start": v(165.1, 171.45) * mm, "end": v(177.8, 171.45) * mm});
            skLineSegment(sketch, "E12.6.7.0", {"start": v(165.1, 196.85) * mm, "end": v(165.1, 203.2) * mm});
            skLineSegment(sketch, "E12.6.7.1", {"start": v(165.1, 203.2) * mm, "end": v(177.8, 203.2) * mm});
            skLineSegment(sketch, "E12.6.7.2", {"start": v(177.8, 196.85) * mm, "end": v(177.8, 203.2) * mm});
            skLineSegment(sketch, "E12.6.7.3", {"start": v(165.1, 196.85) * mm, "end": v(177.8, 196.85) * mm});
            skLineSegment(sketch, "E12.6.8.0", {"start": v(165.1, 222.25) * mm, "end": v(165.1, 228.6) * mm});
            skLineSegment(sketch, "E12.6.8.1", {"start": v(165.1, 228.6) * mm, "end": v(177.8, 228.6) * mm});
            skLineSegment(sketch, "E12.6.8.2", {"start": v(177.8, 222.25) * mm, "end": v(177.8, 228.6) * mm});
            skLineSegment(sketch, "E12.6.8.3", {"start": v(165.1, 222.25) * mm, "end": v(177.8, 222.25) * mm});
            skLineSegment(sketch, "E12.6.9.0", {"start": v(165.1, 247.65) * mm, "end": v(165.1, 254) * mm});
            skLineSegment(sketch, "E12.6.9.1", {"start": v(165.1, 254) * mm, "end": v(177.8, 254) * mm});
            skLineSegment(sketch, "E12.6.9.2", {"start": v(177.8, 247.65) * mm, "end": v(177.8, 254) * mm});
            skLineSegment(sketch, "E12.6.9.3", {"start": v(165.1, 247.65) * mm, "end": v(177.8, 247.65) * mm});
            skLineSegment(sketch, "E12.6.10.0", {"start": v(165.1, 273.05) * mm, "end": v(165.1, 279.4) * mm});
            skLineSegment(sketch, "E12.6.10.1", {"start": v(165.1, 279.4) * mm, "end": v(177.8, 279.4) * mm});
            skLineSegment(sketch, "E12.6.10.2", {"start": v(177.8, 273.05) * mm, "end": v(177.8, 279.4) * mm});
            skLineSegment(sketch, "E12.6.10.3", {"start": v(165.1, 273.05) * mm, "end": v(177.8, 273.05) * mm});
            skLineSegment(sketch, "E12.7.0.0", {"start": v(190.5, 19.05) * mm, "end": v(190.5, 25.4) * mm});
            skLineSegment(sketch, "E12.7.0.1", {"start": v(190.5, 25.4) * mm, "end": v(203.2, 25.4) * mm});
            skLineSegment(sketch, "E12.7.0.2", {"start": v(203.2, 19.05) * mm, "end": v(203.2, 25.4) * mm});
            skLineSegment(sketch, "E12.7.0.3", {"start": v(190.5, 19.05) * mm, "end": v(203.2, 19.05) * mm});
            skLineSegment(sketch, "E12.7.1.0", {"start": v(190.5, 44.45) * mm, "end": v(190.5, 50.8) * mm});
            skLineSegment(sketch, "E12.7.1.1", {"start": v(190.5, 50.8) * mm, "end": v(203.2, 50.8) * mm});
            skLineSegment(sketch, "E12.7.1.2", {"start": v(203.2, 44.45) * mm, "end": v(203.2, 50.8) * mm});
            skLineSegment(sketch, "E12.7.1.3", {"start": v(190.5, 44.45) * mm, "end": v(203.2, 44.45) * mm});
            skLineSegment(sketch, "E12.7.2.0", {"start": v(190.5, 69.85) * mm, "end": v(190.5, 76.2) * mm});
            skLineSegment(sketch, "E12.7.2.1", {"start": v(190.5, 76.2) * mm, "end": v(203.2, 76.2) * mm});
            skLineSegment(sketch, "E12.7.2.2", {"start": v(203.2, 69.85) * mm, "end": v(203.2, 76.2) * mm});
            skLineSegment(sketch, "E12.7.2.3", {"start": v(190.5, 69.85) * mm, "end": v(203.2, 69.85) * mm});
            skLineSegment(sketch, "E12.7.3.0", {"start": v(190.5, 95.25) * mm, "end": v(190.5, 101.6) * mm});
            skLineSegment(sketch, "E12.7.3.1", {"start": v(190.5, 101.6) * mm, "end": v(203.2, 101.6) * mm});
            skLineSegment(sketch, "E12.7.3.2", {"start": v(203.2, 95.25) * mm, "end": v(203.2, 101.6) * mm});
            skLineSegment(sketch, "E12.7.3.3", {"start": v(190.5, 95.25) * mm, "end": v(203.2, 95.25) * mm});
            skLineSegment(sketch, "E12.7.4.0", {"start": v(190.5, 120.65) * mm, "end": v(190.5, 127) * mm});
            skLineSegment(sketch, "E12.7.4.1", {"start": v(190.5, 127) * mm, "end": v(203.2, 127) * mm});
            skLineSegment(sketch, "E12.7.4.2", {"start": v(203.2, 120.65) * mm, "end": v(203.2, 127) * mm});
            skLineSegment(sketch, "E12.7.4.3", {"start": v(190.5, 120.65) * mm, "end": v(203.2, 120.65) * mm});
            skLineSegment(sketch, "E12.7.5.0", {"start": v(190.5, 146.05) * mm, "end": v(190.5, 152.4) * mm});
            skLineSegment(sketch, "E12.7.5.1", {"start": v(190.5, 152.4) * mm, "end": v(203.2, 152.4) * mm});
            skLineSegment(sketch, "E12.7.5.2", {"start": v(203.2, 146.05) * mm, "end": v(203.2, 152.4) * mm});
            skLineSegment(sketch, "E12.7.5.3", {"start": v(190.5, 146.05) * mm, "end": v(203.2, 146.05) * mm});
            skLineSegment(sketch, "E12.7.6.0", {"start": v(190.5, 171.45) * mm, "end": v(190.5, 177.8) * mm});
            skLineSegment(sketch, "E12.7.6.1", {"start": v(190.5, 177.8) * mm, "end": v(203.2, 177.8) * mm});
            skLineSegment(sketch, "E12.7.6.2", {"start": v(203.2, 171.45) * mm, "end": v(203.2, 177.8) * mm});
            skLineSegment(sketch, "E12.7.6.3", {"start": v(190.5, 171.45) * mm, "end": v(203.2, 171.45) * mm});
            skLineSegment(sketch, "E12.7.7.0", {"start": v(190.5, 196.85) * mm, "end": v(190.5, 203.2) * mm});
            skLineSegment(sketch, "E12.7.7.1", {"start": v(190.5, 203.2) * mm, "end": v(203.2, 203.2) * mm});
            skLineSegment(sketch, "E12.7.7.2", {"start": v(203.2, 196.85) * mm, "end": v(203.2, 203.2) * mm});
            skLineSegment(sketch, "E12.7.7.3", {"start": v(190.5, 196.85) * mm, "end": v(203.2, 196.85) * mm});
            skLineSegment(sketch, "E12.7.8.0", {"start": v(190.5, 222.25) * mm, "end": v(190.5, 228.6) * mm});
            skLineSegment(sketch, "E12.7.8.1", {"start": v(190.5, 228.6) * mm, "end": v(203.2, 228.6) * mm});
            skLineSegment(sketch, "E12.7.8.2", {"start": v(203.2, 222.25) * mm, "end": v(203.2, 228.6) * mm});
            skLineSegment(sketch, "E12.7.8.3", {"start": v(190.5, 222.25) * mm, "end": v(203.2, 222.25) * mm});
            skLineSegment(sketch, "E12.7.9.0", {"start": v(190.5, 247.65) * mm, "end": v(190.5, 254) * mm});
            skLineSegment(sketch, "E12.7.9.1", {"start": v(190.5, 254) * mm, "end": v(203.2, 254) * mm});
            skLineSegment(sketch, "E12.7.9.2", {"start": v(203.2, 247.65) * mm, "end": v(203.2, 254) * mm});
            skLineSegment(sketch, "E12.7.9.3", {"start": v(190.5, 247.65) * mm, "end": v(203.2, 247.65) * mm});
            skLineSegment(sketch, "E12.7.10.0", {"start": v(190.5, 273.05) * mm, "end": v(190.5, 279.4) * mm});
            skLineSegment(sketch, "E12.7.10.1", {"start": v(190.5, 279.4) * mm, "end": v(203.2, 279.4) * mm});
            skLineSegment(sketch, "E12.7.10.2", {"start": v(203.2, 273.05) * mm, "end": v(203.2, 279.4) * mm});
            skLineSegment(sketch, "E12.7.10.3", {"start": v(190.5, 273.05) * mm, "end": v(203.2, 273.05) * mm});
            skLineSegment(sketch, "E12.8.0.0", {"start": v(215.9, 19.05) * mm, "end": v(215.9, 25.4) * mm});
            skLineSegment(sketch, "E12.8.0.1", {"start": v(215.9, 25.4) * mm, "end": v(228.6, 25.4) * mm});
            skLineSegment(sketch, "E12.8.0.2", {"start": v(228.6, 19.05) * mm, "end": v(228.6, 25.4) * mm});
            skLineSegment(sketch, "E12.8.0.3", {"start": v(215.9, 19.05) * mm, "end": v(228.6, 19.05) * mm});
            skLineSegment(sketch, "E12.8.1.0", {"start": v(215.9, 44.45) * mm, "end": v(215.9, 50.8) * mm});
            skLineSegment(sketch, "E12.8.1.1", {"start": v(215.9, 50.8) * mm, "end": v(228.6, 50.8) * mm});
            skLineSegment(sketch, "E12.8.1.2", {"start": v(228.6, 44.45) * mm, "end": v(228.6, 50.8) * mm});
            skLineSegment(sketch, "E12.8.1.3", {"start": v(215.9, 44.45) * mm, "end": v(228.6, 44.45) * mm});
            skLineSegment(sketch, "E12.8.2.0", {"start": v(215.9, 69.85) * mm, "end": v(215.9, 76.2) * mm});
            skLineSegment(sketch, "E12.8.2.1", {"start": v(215.9, 76.2) * mm, "end": v(228.6, 76.2) * mm});
            skLineSegment(sketch, "E12.8.2.2", {"start": v(228.6, 69.85) * mm, "end": v(228.6, 76.2) * mm});
            skLineSegment(sketch, "E12.8.2.3", {"start": v(215.9, 69.85) * mm, "end": v(228.6, 69.85) * mm});
            skLineSegment(sketch, "E12.8.3.0", {"start": v(215.9, 95.25) * mm, "end": v(215.9, 101.6) * mm});
            skLineSegment(sketch, "E12.8.3.1", {"start": v(215.9, 101.6) * mm, "end": v(228.6, 101.6) * mm});
            skLineSegment(sketch, "E12.8.3.2", {"start": v(228.6, 95.25) * mm, "end": v(228.6, 101.6) * mm});
            skLineSegment(sketch, "E12.8.3.3", {"start": v(215.9, 95.25) * mm, "end": v(228.6, 95.25) * mm});
            skLineSegment(sketch, "E12.8.4.0", {"start": v(215.9, 120.65) * mm, "end": v(215.9, 127) * mm});
            skLineSegment(sketch, "E12.8.4.1", {"start": v(215.9, 127) * mm, "end": v(228.6, 127) * mm});
            skLineSegment(sketch, "E12.8.4.2", {"start": v(228.6, 120.65) * mm, "end": v(228.6, 127) * mm});
            skLineSegment(sketch, "E12.8.4.3", {"start": v(215.9, 120.65) * mm, "end": v(228.6, 120.65) * mm});
            skLineSegment(sketch, "E12.8.5.0", {"start": v(215.9, 146.05) * mm, "end": v(215.9, 152.4) * mm});
            skLineSegment(sketch, "E12.8.5.1", {"start": v(215.9, 152.4) * mm, "end": v(228.6, 152.4) * mm});
            skLineSegment(sketch, "E12.8.5.2", {"start": v(228.6, 146.05) * mm, "end": v(228.6, 152.4) * mm});
            skLineSegment(sketch, "E12.8.5.3", {"start": v(215.9, 146.05) * mm, "end": v(228.6, 146.05) * mm});
            skLineSegment(sketch, "E12.8.6.0", {"start": v(215.9, 171.45) * mm, "end": v(215.9, 177.8) * mm});
            skLineSegment(sketch, "E12.8.6.1", {"start": v(215.9, 177.8) * mm, "end": v(228.6, 177.8) * mm});
            skLineSegment(sketch, "E12.8.6.2", {"start": v(228.6, 171.45) * mm, "end": v(228.6, 177.8) * mm});
            skLineSegment(sketch, "E12.8.6.3", {"start": v(215.9, 171.45) * mm, "end": v(228.6, 171.45) * mm});
            skLineSegment(sketch, "E12.8.7.0", {"start": v(215.9, 196.85) * mm, "end": v(215.9, 203.2) * mm});
            skLineSegment(sketch, "E12.8.7.1", {"start": v(215.9, 203.2) * mm, "end": v(228.6, 203.2) * mm});
            skLineSegment(sketch, "E12.8.7.2", {"start": v(228.6, 196.85) * mm, "end": v(228.6, 203.2) * mm});
            skLineSegment(sketch, "E12.8.7.3", {"start": v(215.9, 196.85) * mm, "end": v(228.6, 196.85) * mm});
            skLineSegment(sketch, "E12.8.8.0", {"start": v(215.9, 222.25) * mm, "end": v(215.9, 228.6) * mm});
            skLineSegment(sketch, "E12.8.8.1", {"start": v(215.9, 228.6) * mm, "end": v(228.6, 228.6) * mm});
            skLineSegment(sketch, "E12.8.8.2", {"start": v(228.6, 222.25) * mm, "end": v(228.6, 228.6) * mm});
            skLineSegment(sketch, "E12.8.8.3", {"start": v(215.9, 222.25) * mm, "end": v(228.6, 222.25) * mm});
            skLineSegment(sketch, "E12.8.9.0", {"start": v(215.9, 247.65) * mm, "end": v(215.9, 254) * mm});
            skLineSegment(sketch, "E12.8.9.1", {"start": v(215.9, 254) * mm, "end": v(228.6, 254) * mm});
            skLineSegment(sketch, "E12.8.9.2", {"start": v(228.6, 247.65) * mm, "end": v(228.6, 254) * mm});
            skLineSegment(sketch, "E12.8.9.3", {"start": v(215.9, 247.65) * mm, "end": v(228.6, 247.65) * mm});
            skLineSegment(sketch, "E12.8.10.0", {"start": v(215.9, 273.05) * mm, "end": v(215.9, 279.4) * mm});
            skLineSegment(sketch, "E12.8.10.1", {"start": v(215.9, 279.4) * mm, "end": v(228.6, 279.4) * mm});
            skLineSegment(sketch, "E12.8.10.2", {"start": v(228.6, 273.05) * mm, "end": v(228.6, 279.4) * mm});
            skLineSegment(sketch, "E12.8.10.3", {"start": v(215.9, 273.05) * mm, "end": v(228.6, 273.05) * mm});
            skLineSegment(sketch, "E12.9.0.0", {"start": v(241.3, 19.05) * mm, "end": v(241.3, 25.4) * mm});
            skLineSegment(sketch, "E12.9.0.1", {"start": v(241.3, 25.4) * mm, "end": v(254, 25.4) * mm});
            skLineSegment(sketch, "E12.9.0.2", {"start": v(254, 19.05) * mm, "end": v(254, 25.4) * mm});
            skLineSegment(sketch, "E12.9.0.3", {"start": v(241.3, 19.05) * mm, "end": v(254, 19.05) * mm});
            skLineSegment(sketch, "E12.9.1.0", {"start": v(241.3, 44.45) * mm, "end": v(241.3, 50.8) * mm});
            skLineSegment(sketch, "E12.9.1.1", {"start": v(241.3, 50.8) * mm, "end": v(254, 50.8) * mm});
            skLineSegment(sketch, "E12.9.1.2", {"start": v(254, 44.45) * mm, "end": v(254, 50.8) * mm});
            skLineSegment(sketch, "E12.9.1.3", {"start": v(241.3, 44.45) * mm, "end": v(254, 44.45) * mm});
            skLineSegment(sketch, "E12.9.2.0", {"start": v(241.3, 69.85) * mm, "end": v(241.3, 76.2) * mm});
            skLineSegment(sketch, "E12.9.2.1", {"start": v(241.3, 76.2) * mm, "end": v(254, 76.2) * mm});
            skLineSegment(sketch, "E12.9.2.2", {"start": v(254, 69.85) * mm, "end": v(254, 76.2) * mm});
            skLineSegment(sketch, "E12.9.2.3", {"start": v(241.3, 69.85) * mm, "end": v(254, 69.85) * mm});
            skLineSegment(sketch, "E12.9.3.0", {"start": v(241.3, 95.25) * mm, "end": v(241.3, 101.6) * mm});
            skLineSegment(sketch, "E12.9.3.1", {"start": v(241.3, 101.6) * mm, "end": v(254, 101.6) * mm});
            skLineSegment(sketch, "E12.9.3.2", {"start": v(254, 95.25) * mm, "end": v(254, 101.6) * mm});
            skLineSegment(sketch, "E12.9.3.3", {"start": v(241.3, 95.25) * mm, "end": v(254, 95.25) * mm});
            skLineSegment(sketch, "E12.9.4.0", {"start": v(241.3, 120.65) * mm, "end": v(241.3, 127) * mm});
            skLineSegment(sketch, "E12.9.4.1", {"start": v(241.3, 127) * mm, "end": v(254, 127) * mm});
            skLineSegment(sketch, "E12.9.4.2", {"start": v(254, 120.65) * mm, "end": v(254, 127) * mm});
            skLineSegment(sketch, "E12.9.4.3", {"start": v(241.3, 120.65) * mm, "end": v(254, 120.65) * mm});
            skLineSegment(sketch, "E12.9.5.0", {"start": v(241.3, 146.05) * mm, "end": v(241.3, 152.4) * mm});
            skLineSegment(sketch, "E12.9.5.1", {"start": v(241.3, 152.4) * mm, "end": v(254, 152.4) * mm});
            skLineSegment(sketch, "E12.9.5.2", {"start": v(254, 146.05) * mm, "end": v(254, 152.4) * mm});
            skLineSegment(sketch, "E12.9.5.3", {"start": v(241.3, 146.05) * mm, "end": v(254, 146.05) * mm});
            skLineSegment(sketch, "E12.9.6.0", {"start": v(241.3, 171.45) * mm, "end": v(241.3, 177.8) * mm});
            skLineSegment(sketch, "E12.9.6.1", {"start": v(241.3, 177.8) * mm, "end": v(254, 177.8) * mm});
            skLineSegment(sketch, "E12.9.6.2", {"start": v(254, 171.45) * mm, "end": v(254, 177.8) * mm});
            skLineSegment(sketch, "E12.9.6.3", {"start": v(241.3, 171.45) * mm, "end": v(254, 171.45) * mm});
            skLineSegment(sketch, "E12.9.7.0", {"start": v(241.3, 196.85) * mm, "end": v(241.3, 203.2) * mm});
            skLineSegment(sketch, "E12.9.7.1", {"start": v(241.3, 203.2) * mm, "end": v(254, 203.2) * mm});
            skLineSegment(sketch, "E12.9.7.2", {"start": v(254, 196.85) * mm, "end": v(254, 203.2) * mm});
            skLineSegment(sketch, "E12.9.7.3", {"start": v(241.3, 196.85) * mm, "end": v(254, 196.85) * mm});
            skLineSegment(sketch, "E12.9.8.0", {"start": v(241.3, 222.25) * mm, "end": v(241.3, 228.6) * mm});
            skLineSegment(sketch, "E12.9.8.1", {"start": v(241.3, 228.6) * mm, "end": v(254, 228.6) * mm});
            skLineSegment(sketch, "E12.9.8.2", {"start": v(254, 222.25) * mm, "end": v(254, 228.6) * mm});
            skLineSegment(sketch, "E12.9.8.3", {"start": v(241.3, 222.25) * mm, "end": v(254, 222.25) * mm});
            skLineSegment(sketch, "E12.9.9.0", {"start": v(241.3, 247.65) * mm, "end": v(241.3, 254) * mm});
            skLineSegment(sketch, "E12.9.9.1", {"start": v(241.3, 254) * mm, "end": v(254, 254) * mm});
            skLineSegment(sketch, "E12.9.9.2", {"start": v(254, 247.65) * mm, "end": v(254, 254) * mm});
            skLineSegment(sketch, "E12.9.9.3", {"start": v(241.3, 247.65) * mm, "end": v(254, 247.65) * mm});
            skLineSegment(sketch, "E12.9.10.0", {"start": v(241.3, 273.05) * mm, "end": v(241.3, 279.4) * mm});
            skLineSegment(sketch, "E12.9.10.1", {"start": v(241.3, 279.4) * mm, "end": v(254, 279.4) * mm});
            skLineSegment(sketch, "E12.9.10.2", {"start": v(254, 273.05) * mm, "end": v(254, 279.4) * mm});
            skLineSegment(sketch, "E12.9.10.3", {"start": v(241.3, 273.05) * mm, "end": v(254, 273.05) * mm});
            skLineSegment(sketch, "E12.10.0.0", {"start": v(266.7, 19.05) * mm, "end": v(266.7, 25.4) * mm});
            skLineSegment(sketch, "E12.10.0.1", {"start": v(266.7, 25.4) * mm, "end": v(279.4, 25.4) * mm});
            skLineSegment(sketch, "E12.10.0.2", {"start": v(279.4, 19.05) * mm, "end": v(279.4, 25.4) * mm});
            skLineSegment(sketch, "E12.10.0.3", {"start": v(266.7, 19.05) * mm, "end": v(279.4, 19.05) * mm});
            skLineSegment(sketch, "E12.10.1.0", {"start": v(266.7, 44.45) * mm, "end": v(266.7, 50.8) * mm});
            skLineSegment(sketch, "E12.10.1.1", {"start": v(266.7, 50.8) * mm, "end": v(279.4, 50.8) * mm});
            skLineSegment(sketch, "E12.10.1.2", {"start": v(279.4, 44.45) * mm, "end": v(279.4, 50.8) * mm});
            skLineSegment(sketch, "E12.10.1.3", {"start": v(266.7, 44.45) * mm, "end": v(279.4, 44.45) * mm});
            skLineSegment(sketch, "E12.10.2.0", {"start": v(266.7, 69.85) * mm, "end": v(266.7, 76.2) * mm});
            skLineSegment(sketch, "E12.10.2.1", {"start": v(266.7, 76.2) * mm, "end": v(279.4, 76.2) * mm});
            skLineSegment(sketch, "E12.10.2.2", {"start": v(279.4, 69.85) * mm, "end": v(279.4, 76.2) * mm});
            skLineSegment(sketch, "E12.10.2.3", {"start": v(266.7, 69.85) * mm, "end": v(279.4, 69.85) * mm});
            skLineSegment(sketch, "E12.10.3.0", {"start": v(266.7, 95.25) * mm, "end": v(266.7, 101.6) * mm});
            skLineSegment(sketch, "E12.10.3.1", {"start": v(266.7, 101.6) * mm, "end": v(279.4, 101.6) * mm});
            skLineSegment(sketch, "E12.10.3.2", {"start": v(279.4, 95.25) * mm, "end": v(279.4, 101.6) * mm});
            skLineSegment(sketch, "E12.10.3.3", {"start": v(266.7, 95.25) * mm, "end": v(279.4, 95.25) * mm});
            skLineSegment(sketch, "E12.10.4.0", {"start": v(266.7, 120.65) * mm, "end": v(266.7, 127) * mm});
            skLineSegment(sketch, "E12.10.4.1", {"start": v(266.7, 127) * mm, "end": v(279.4, 127) * mm});
            skLineSegment(sketch, "E12.10.4.2", {"start": v(279.4, 120.65) * mm, "end": v(279.4, 127) * mm});
            skLineSegment(sketch, "E12.10.4.3", {"start": v(266.7, 120.65) * mm, "end": v(279.4, 120.65) * mm});
            skLineSegment(sketch, "E12.10.5.0", {"start": v(266.7, 146.05) * mm, "end": v(266.7, 152.4) * mm});
            skLineSegment(sketch, "E12.10.5.1", {"start": v(266.7, 152.4) * mm, "end": v(279.4, 152.4) * mm});
            skLineSegment(sketch, "E12.10.5.2", {"start": v(279.4, 146.05) * mm, "end": v(279.4, 152.4) * mm});
            skLineSegment(sketch, "E12.10.5.3", {"start": v(266.7, 146.05) * mm, "end": v(279.4, 146.05) * mm});
            skLineSegment(sketch, "E12.10.6.0", {"start": v(266.7, 171.45) * mm, "end": v(266.7, 177.8) * mm});
            skLineSegment(sketch, "E12.10.6.1", {"start": v(266.7, 177.8) * mm, "end": v(279.4, 177.8) * mm});
            skLineSegment(sketch, "E12.10.6.2", {"start": v(279.4, 171.45) * mm, "end": v(279.4, 177.8) * mm});
            skLineSegment(sketch, "E12.10.6.3", {"start": v(266.7, 171.45) * mm, "end": v(279.4, 171.45) * mm});
            skLineSegment(sketch, "E12.10.7.0", {"start": v(266.7, 196.85) * mm, "end": v(266.7, 203.2) * mm});
            skLineSegment(sketch, "E12.10.7.1", {"start": v(266.7, 203.2) * mm, "end": v(279.4, 203.2) * mm});
            skLineSegment(sketch, "E12.10.7.2", {"start": v(279.4, 196.85) * mm, "end": v(279.4, 203.2) * mm});
            skLineSegment(sketch, "E12.10.7.3", {"start": v(266.7, 196.85) * mm, "end": v(279.4, 196.85) * mm});
            skLineSegment(sketch, "E12.10.8.0", {"start": v(266.7, 222.25) * mm, "end": v(266.7, 228.6) * mm});
            skLineSegment(sketch, "E12.10.8.1", {"start": v(266.7, 228.6) * mm, "end": v(279.4, 228.6) * mm});
            skLineSegment(sketch, "E12.10.8.2", {"start": v(279.4, 222.25) * mm, "end": v(279.4, 228.6) * mm});
            skLineSegment(sketch, "E12.10.8.3", {"start": v(266.7, 222.25) * mm, "end": v(279.4, 222.25) * mm});
            skLineSegment(sketch, "E12.10.9.0", {"start": v(266.7, 247.65) * mm, "end": v(266.7, 254) * mm});
            skLineSegment(sketch, "E12.10.9.1", {"start": v(266.7, 254) * mm, "end": v(279.4, 254) * mm});
            skLineSegment(sketch, "E12.10.9.2", {"start": v(279.4, 247.65) * mm, "end": v(279.4, 254) * mm});
            skLineSegment(sketch, "E12.10.9.3", {"start": v(266.7, 247.65) * mm, "end": v(279.4, 247.65) * mm});
            skLineSegment(sketch, "E12.10.10.0", {"start": v(266.7, 273.05) * mm, "end": v(266.7, 279.4) * mm});
            skLineSegment(sketch, "E12.10.10.1", {"start": v(266.7, 279.4) * mm, "end": v(279.4, 279.4) * mm});
            skLineSegment(sketch, "E12.10.10.2", {"start": v(279.4, 273.05) * mm, "end": v(279.4, 279.4) * mm});
            skLineSegment(sketch, "E12.10.10.3", {"start": v(266.7, 273.05) * mm, "end": v(279.4, 273.05) * mm});
            skLineSegment(sketch, "E12.direction1", {"start": v(12.7, 19.05) * mm, "end": v(38.1, 19.05) * mm, "construction": true});
            skLineSegment(sketch, "E12.direction2", {"start": v(12.7, 19.05) * mm, "end": v(12.7, 44.45) * mm, "construction": true});
            skSolve(sketch);
        }
        {
            var Q0;
            Q0 = qSketchRegion(id + "F2", true);
            extrude(context, id + "F3", {"entities" : qUnion([Q0]), "operationType" : NewBodyOperationType.REMOVE, "oppositeDirection" : true, "depth" : 317.5 * mm, "offsetDistance" : 25.4 * mm});
        }
    });
